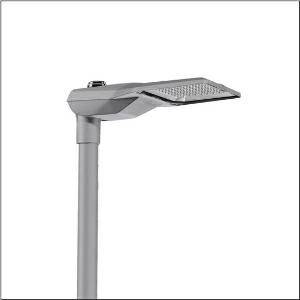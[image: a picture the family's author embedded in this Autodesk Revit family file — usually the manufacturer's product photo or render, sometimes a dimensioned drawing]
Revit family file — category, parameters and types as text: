
# Revit family: streetlight_sl_21_midi___st1_5a_5xe7p37n08mb_d4f4
name_source: partatom
category: Lighting Fixtures
units: mm (PartAtom-declared; Revit-internal decimal feet)

## family parameters
Cut with Voids When Loaded = No
Host = Face
Light Source = No
Part Type = Normal
Room Calculation Point = No
Round Connector Dimension = Use Diameter
Shared = No

## types (1)
- --- (1 x LED, 17960 lm, 136 W, 3000K)
    Apparent Load = 136 VA
    CIE Flux Codes = 22 53 95 100 100
    Color Rendering = 70
    Color Temperature = 3000K
    Default Elevation = 1800 mm
    Description = Streetlight SL 21 midi, mast luminaire, primary light control with lens, of PMMA, primary optical cover: cover, of toughened safety glass, transparent, light distribution: ST1.5a, light emission: direct distribution, primary light characteristic: asymmetric, installation type: side-entry, LED, 3G 2.5mm², High Power LED, rated luminous flux: 17.960lm, luminous efficacy: 132lm/W, light colour: 730, colour temperature: 3000K, control: overheat protection, presetting dimming linear, constant luminous flux control, time-dependent luminous flux control, flexible luminous flux parameterisation, mains connection: 220..240V, AC, 50/60Hz, connection cable pre-assembled, cable length: 12,5m, wiring characteristics: H05VV-F, start of lifetime: 136W, end of service life: 142W, reduction: 61W, luminaire housing, of diecast aluminium (EN AC-44300), powder-coated, Siteco® metallic grey (DB 702S), corrosivity category C5 mid according to DIN EN ISO 12944, multi-level sealing system, sealing non-destructively replaceable, inclination adjustable: 0°, 5°, 10°, 15°, length: 644mm, width: 335mm, height: 110mm, spigot size: 42mm (side-entry), protection rating (complete): IP66, insulation class (complete): insulation class I (protective earthing), certification: CE, ENEC, ENEC+, VDE, impact resistance: IK09, permissible operating ambient temperature for outdoor applications: -40..+50°C, standard-compliant lighting for roads and squares, packaging unit: 1 piece

Light Distribution: ST1.5a
    Height = 111 mm
    Lamp = 1 x LED
    Lamp Light Flux = 17960 lm
    Lamp Power = 136 W
    Lamp count = 1
    Length = 644 mm
    Luminous efficacy = 132 lm/W
    Manufacturer = Siteco
    ModVariant = No
    Model = 5XE7P37N08MB
    Number of Poles = 1
    OnlyDefault = Yes
    Power Factor = 1
    Product Name = Streetlight SL 21 midi | ST1.5a
    Product group = mast luminaire | pylon top
    ProductGroupID = 6100
    Protection Class = Protection class I
    Protection Degree = IP 66
    RLX_Detail_Level = 1
    RLX_Emergency_Light_Flux = 0 lm
    RLX_Emergency_Type = 0
    RLX_Emergency_Type_DB = No
    RlxData = <blob elided: 94333 chars, md5=618e9e3e>
    Socket = socket
    Standby Power = 0 W
    System Light Flux = 17960 lm
    System Power = 136 W
    Type Comments = factory setting: luminous flux: 100 % | dim-lin: 254 | 695 mA
    Type Image = l_1294377.jpg
    URL = http://relux.com
    VarID = @adj_082839
    Voltage = 0 V
    Weight = 0.00 kg
    Width = 336 mm

## geometry (parser evidence)
native form markers: Blend x4, Sweep x12
no freeform markers — native parametric forms only
